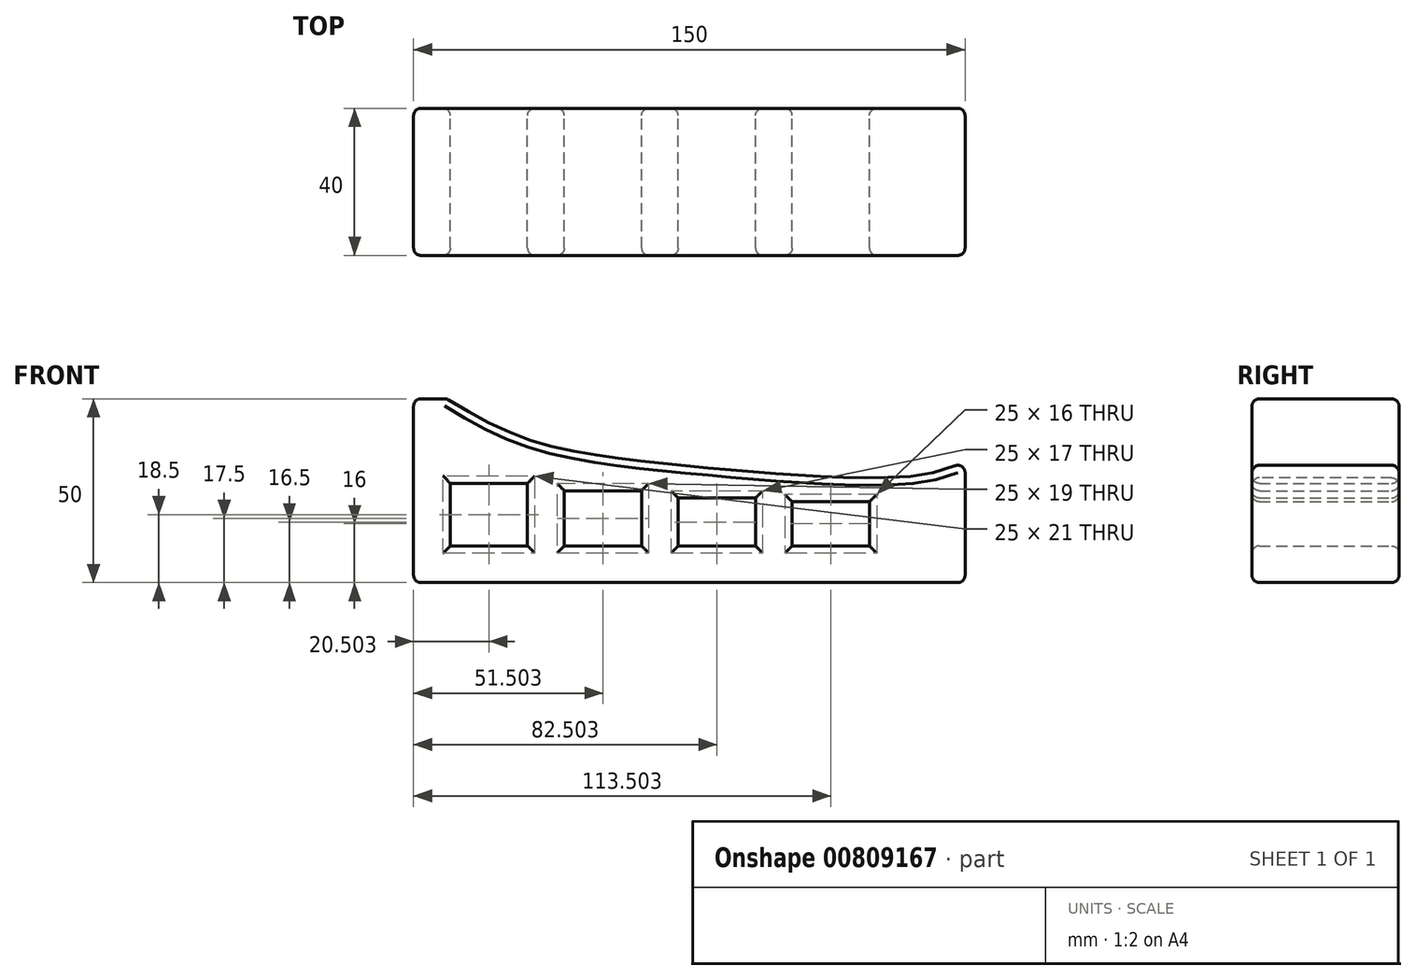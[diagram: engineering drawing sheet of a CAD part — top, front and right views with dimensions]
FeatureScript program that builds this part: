
annotation { "Feature Type Name" : "Feature", "Feature Type Description" : "" }
export const myFeature = defineFeature(function(context is Context, id is Id, definition is map)
    precondition{}
    {
        {
            var Q0;
            Q0=qCreatedBy(makeId("Front.planeOp"),FACE);
            var sketch = newSketch(context, id + "F0", { "sketchPlane" : qUnion([Q0])});
            skLineSegment(sketch, "E0.bottom", {"start": v(-187.73, 0) * mm, "end": v(-37.73, 0) * mm});
            skLineSegment(sketch, "E0.top", {"start": v(-187.73, 50) * mm, "end": v(-178.73, 50) * mm});
            skLineSegment(sketch, "E0.left", {"start": v(-187.73, 0) * mm, "end": v(-187.73, 50) * mm});
            skLineSegment(sketch, "E0.right", {"start": v(-37.73, 0) * mm, "end": v(-37.73, 33) * mm});
            skLineSegment(sketch, "E1", {"start": v(-187.73, 0) * mm, "end": v(-177.73, 0) * mm});
            skLineSegment(sketch, "E2", {"start": v(-177.73, 0) * mm, "end": v(-156.73, 0) * mm});
            skLineSegment(sketch, "E3", {"start": v(-156.73, 0) * mm, "end": v(-146.73, 0) * mm});
            skLineSegment(sketch, "E4", {"start": v(-146.73, 0) * mm, "end": v(-125.73, 0) * mm});
            skLineSegment(sketch, "E5", {"start": v(-125.73, 0) * mm, "end": v(-115.73, 0) * mm});
            skLineSegment(sketch, "E6", {"start": v(-115.73, 0) * mm, "end": v(-94.73, 0) * mm});
            skLineSegment(sketch, "E7", {"start": v(-94.73, 0) * mm, "end": v(-84.73, 0) * mm});
            skLineSegment(sketch, "E8", {"start": v(-84.73, 0) * mm, "end": v(-63.73, 0) * mm});
            skLineSegment(sketch, "E9", {"start": v(-187.73, 0) * mm, "end": v(-187.73, 10) * mm});
            skLineSegment(sketch, "E10", {"start": v(-177.73, 10) * mm, "end": v(-156.73, 10) * mm});
            skLineSegment(sketch, "E11", {"start": v(-177.73, 10) * mm, "end": v(-177.73, 27) * mm});
            skLineSegment(sketch, "E12", {"start": v(-177.73, 27) * mm, "end": v(-156.73, 27) * mm});
            skLineSegment(sketch, "E13", {"start": v(-156.73, 27) * mm, "end": v(-156.73, 10) * mm});
            skLineSegment(sketch, "E14", {"start": v(-146.73, 10) * mm, "end": v(-146.73, 25) * mm});
            skLineSegment(sketch, "E15", {"start": v(-146.73, 25) * mm, "end": v(-125.73, 25) * mm});
            skLineSegment(sketch, "E16", {"start": v(-125.73, 25) * mm, "end": v(-125.73, 10) * mm});
            skLineSegment(sketch, "E17", {"start": v(-115.73, 10) * mm, "end": v(-115.73, 23) * mm});
            skLineSegment(sketch, "E18", {"start": v(-115.73, 23) * mm, "end": v(-94.73, 23) * mm});
            skLineSegment(sketch, "E19", {"start": v(-94.73, 23) * mm, "end": v(-94.73, 10) * mm});
            skLineSegment(sketch, "E20", {"start": v(-84.73, 10) * mm, "end": v(-84.73, 22) * mm});
            skLineSegment(sketch, "E21", {"start": v(-84.73, 22) * mm, "end": v(-63.73, 22) * mm});
            skLineSegment(sketch, "E22", {"start": v(-63.73, 22) * mm, "end": v(-63.73, 10) * mm});
            skLineSegment(sketch, "E23", {"start": v(-37.73, 0) * mm, "end": v(-51.73, 0) * mm});
            skLineSegment(sketch, "E24", {"start": v(-37.73, 0) * mm, "end": v(-115.73, 0) * mm});
            skLineSegment(sketch, "E25", {"start": v(-156.73, 10) * mm, "end": v(-156.73, 27) * mm});
            skFitSpline(sketch, "E26", {"points": [v(-178.73, 50) * mm, v(-156.73, 39) * mm, v(-115.73, 32) * mm, v(-51.73, 29) * mm, v(-37.73, 33) * mm], "startDerivative": vector(96.63, -58.6) * mm, "endDerivative": vector(65.87, 30.7) * mm});
            skLineSegment(sketch, "E27.trimOffspring", {"start": v(-84.73, 10) * mm, "end": v(-63.73, 10) * mm});
            skLineSegment(sketch, "E28.trimOffspring", {"start": v(-115.73, 10) * mm, "end": v(-94.73, 10) * mm});
            skLineSegment(sketch, "E29.trimOffspring", {"start": v(-146.73, 10) * mm, "end": v(-125.73, 10) * mm});
            skLineSegment(sketch, "E30", {"start": v(-178.73, 50) * mm, "end": v(-37.73, 50) * mm});
            skLineSegment(sketch, "E31", {"start": v(-37.73, 50) * mm, "end": v(-37.73, 33) * mm});
            skSolve(sketch);
        }
        {
            var Q0;
            Q0=makeQuery(id+"F0.imprint","IMPRINT",FACE,{"disambiguationData":[TD([[makeQuery(id+"F0.imprint","IMPRINT",EDGE,{"derivedFrom":sQuery(id+"F0.wireOp",EDGE,"E0.left")}),-1.0]])]});
            extrude(context, id + "F1", {"entities" : qUnion([Q0]), "depth" : 40 * mm, "offsetDistance" : 25 * mm});
        }
        {
            var Q0;
            Q0=makeQuery(id+"F1.opExtrude","CAP_FACE",FACE,{"disambiguationData":[OSD([sQuery(id+"F0.wireOp",EDGE,"E0.left"),sQuery(id+"F0.wireOp",EDGE,"E0.top"),sQuery(id+"F0.wireOp",EDGE,"E0.right"),sQuery(id+"F0.wireOp",EDGE,"E1"),sQuery(id+"F0.wireOp",EDGE,"E2"),sQuery(id+"F0.wireOp",EDGE,"E3"),sQuery(id+"F0.wireOp",EDGE,"E4"),sQuery(id+"F0.wireOp",EDGE,"E5"),sQuery(id+"F0.wireOp",EDGE,"E9"),sQuery(id+"F0.wireOp",EDGE,"E10"),sQuery(id+"F0.wireOp",EDGE,"E11"),sQuery(id+"F0.wireOp",EDGE,"E12"),sQuery(id+"F0.wireOp",EDGE,"E14"),sQuery(id+"F0.wireOp",EDGE,"E15"),sQuery(id+"F0.wireOp",EDGE,"E16"),sQuery(id+"F0.wireOp",EDGE,"E18"),sQuery(id+"F0.wireOp",EDGE,"E19"),sQuery(id+"F0.wireOp",EDGE,"E20"),sQuery(id+"F0.wireOp",EDGE,"E21"),sQuery(id+"F0.wireOp",EDGE,"E22"),sQuery(id+"F0.wireOp",EDGE,"E24"),sQuery(id+"F0.wireOp",EDGE,"E17"),sQuery(id+"F0.wireOp",EDGE,"E25"),sQuery(id+"F0.wireOp",EDGE,"E26"),sQuery(id+"F0.wireOp",EDGE,"E27.trimOffspring"),sQuery(id+"F0.wireOp",EDGE,"E28.trimOffspring"),sQuery(id+"F0.wireOp",EDGE,"E29.trimOffspring")])],"isStart":false});
            var Q1;
            Q1=makeQuery(id+"F1.opExtrude","SWEPT_FACE",FACE,{"disambiguationData":[OSD([sQuery(id+"F0.wireOp",EDGE,"E26")])]});
            var Q2;
            Q2=makeQuery(id+"F1.opExtrude","SWEPT_FACE",FACE,{"disambiguationData":[OSD([sQuery(id+"F0.wireOp",EDGE,"E0.left"),sQuery(id+"F0.wireOp",EDGE,"E9")])]});
            var Q3;
            Q3=makeQuery(id+"F1.opExtrude","CAP_FACE",FACE,{"disambiguationData":[OSD([sQuery(id+"F0.wireOp",EDGE,"E0.left"),sQuery(id+"F0.wireOp",EDGE,"E0.top"),sQuery(id+"F0.wireOp",EDGE,"E0.right"),sQuery(id+"F0.wireOp",EDGE,"E1"),sQuery(id+"F0.wireOp",EDGE,"E2"),sQuery(id+"F0.wireOp",EDGE,"E3"),sQuery(id+"F0.wireOp",EDGE,"E4"),sQuery(id+"F0.wireOp",EDGE,"E5"),sQuery(id+"F0.wireOp",EDGE,"E9"),sQuery(id+"F0.wireOp",EDGE,"E10"),sQuery(id+"F0.wireOp",EDGE,"E11"),sQuery(id+"F0.wireOp",EDGE,"E12"),sQuery(id+"F0.wireOp",EDGE,"E14"),sQuery(id+"F0.wireOp",EDGE,"E15"),sQuery(id+"F0.wireOp",EDGE,"E16"),sQuery(id+"F0.wireOp",EDGE,"E18"),sQuery(id+"F0.wireOp",EDGE,"E19"),sQuery(id+"F0.wireOp",EDGE,"E20"),sQuery(id+"F0.wireOp",EDGE,"E21"),sQuery(id+"F0.wireOp",EDGE,"E22"),sQuery(id+"F0.wireOp",EDGE,"E24"),sQuery(id+"F0.wireOp",EDGE,"E17"),sQuery(id+"F0.wireOp",EDGE,"E25"),sQuery(id+"F0.wireOp",EDGE,"E26"),sQuery(id+"F0.wireOp",EDGE,"E27.trimOffspring"),sQuery(id+"F0.wireOp",EDGE,"E28.trimOffspring"),sQuery(id+"F0.wireOp",EDGE,"E29.trimOffspring")])],"isStart":true});
            var Q4;
            Q4=makeQuery(id+"F1.opExtrude","SWEPT_FACE",FACE,{"disambiguationData":[OSD([sQuery(id+"F0.wireOp",EDGE,"E0.right")])]});
            fillet(context, id + "F2", {"entities" : qUnion([Q0, Q1, Q2, Q3, Q4]), "radius" : 2 * mm, "tangentPropagation" : true, "allowEdgeOverflow" : false});
        }
    });
